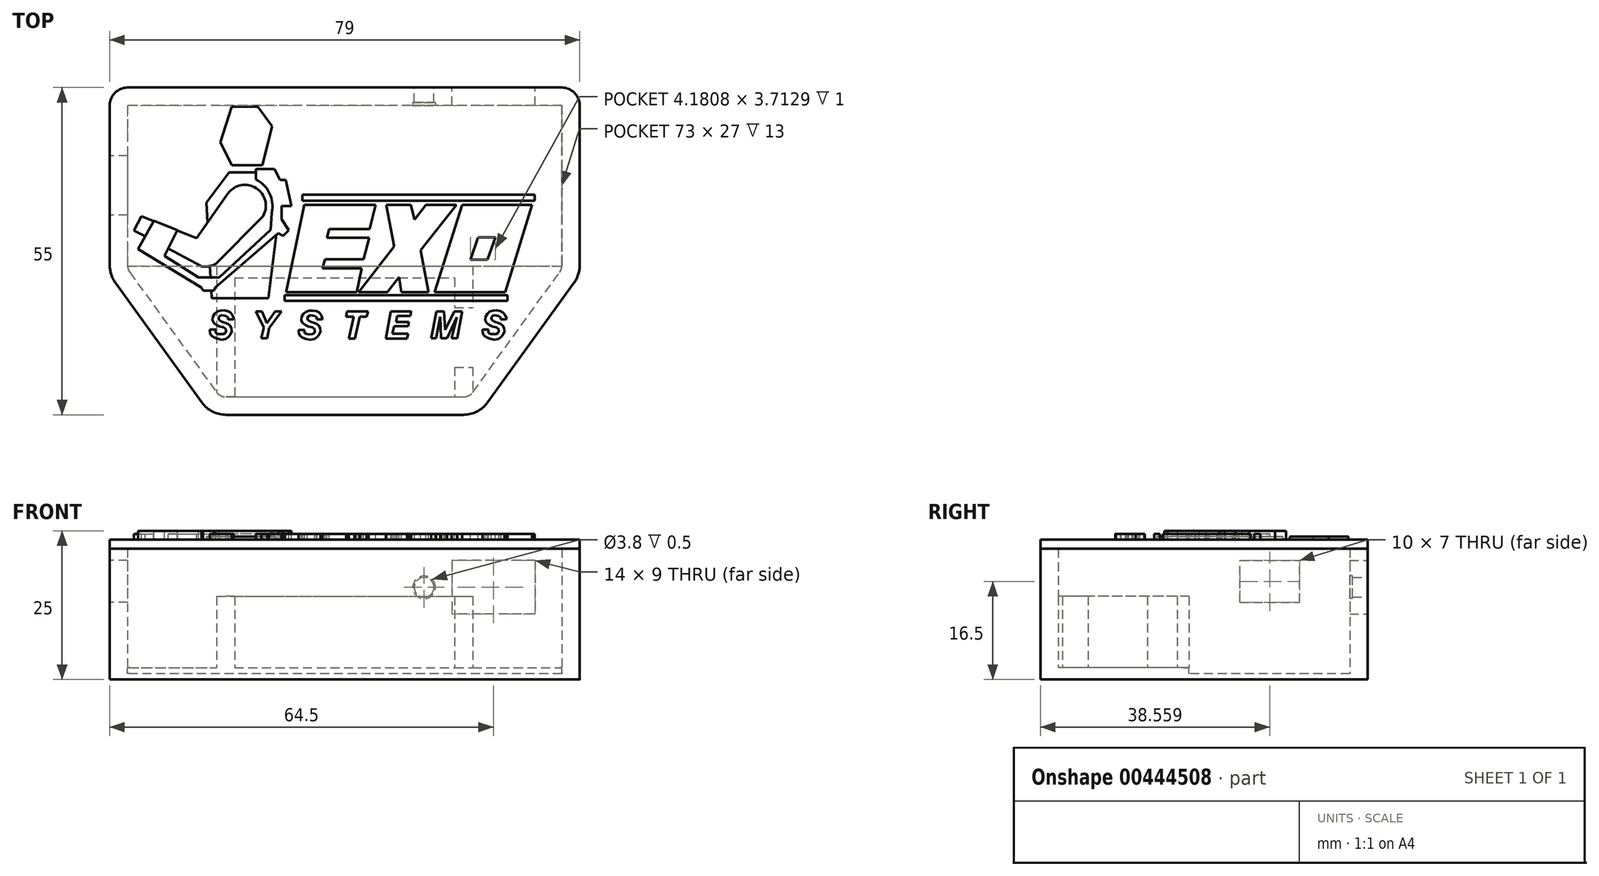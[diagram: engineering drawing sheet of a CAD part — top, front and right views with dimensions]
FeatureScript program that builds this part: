
annotation { "Feature Type Name" : "Feature", "Feature Type Description" : "" }
export const myFeature = defineFeature(function(context is Context, id is Id, definition is map)
    precondition{}
    {
        {
            var Q0;
            Q0=qCreatedBy(makeId("Top.planeOp"),FACE);
            var sketch = newSketch(context, id + "F0", { "sketchPlane" : qUnion([Q0])});
            skLineSegment(sketch, "E0", {"start": v(67, 30) * mm, "end": v(-67, 30) * mm, "construction": true});
            skPoint(sketch, "E1", {"position": v(0, -28) * mm});
            skPoint(sketch, "E2", {"position": v(0, 30) * mm});
            skLineSegment(sketch, "E3.0", {"start": v(36.5, 27) * mm, "end": v(-36.5, 27) * mm});
            skPoint(sketch, "E4.visualSharp", {"position": v(-61.92, 27) * mm});
            skPoint(sketch, "E5.visualSharp", {"position": v(61.92, 27) * mm});
            skLineSegment(sketch, "E6", {"start": v(39.5, 24) * mm, "end": v(39.5, -2.88) * mm});
            skLineSegment(sketch, "E7", {"start": v(38.55, -5.81) * mm, "end": v(24, -25.93) * mm});
            skLineSegment(sketch, "E8", {"start": v(19.95, -28) * mm, "end": v(0, -28) * mm});
            skPoint(sketch, "E9.visualSharp", {"position": v(39.5, -4.5) * mm});
            skArc(sketch, "E9.filletArc", {"start": v(38.55, -5.81) * mm, "mid": v(39.26, -4.42) * mm, "end": v(39.5, -2.88) * mm});
            skPoint(sketch, "E10.visualSharp", {"position": v(22.5, -28) * mm});
            skArc(sketch, "E10.filletArc", {"start": v(19.95, -28) * mm, "mid": v(22.22, -27.45) * mm, "end": v(24, -25.93) * mm});
            skLineSegment(sketch, "E11.MirrorCS", {"start": v(-39.5, 24) * mm, "end": v(-39.5, -2.88) * mm});
            skLineSegment(sketch, "E12.MirrorCS", {"start": v(-38.55, -5.81) * mm, "end": v(-24, -25.93) * mm});
            skLineSegment(sketch, "E13.MirrorCS", {"start": v(-19.95, -28) * mm, "end": v(0, -28) * mm});
            skArc(sketch, "E14.MirrorCS", {"start": v(-19.95, -28) * mm, "mid": v(-22.22, -27.45) * mm, "end": v(-24, -25.93) * mm});
            skArc(sketch, "E15.MirrorCS", {"start": v(-38.55, -5.81) * mm, "mid": v(-39.26, -4.42) * mm, "end": v(-39.5, -2.88) * mm});
            skPoint(sketch, "E16.visualSharp", {"position": v(-39.5, 27) * mm});
            skArc(sketch, "E16.filletArc", {"start": v(-36.5, 27) * mm, "mid": v(-38.62, 26.12) * mm, "end": v(-39.5, 24) * mm});
            skPoint(sketch, "E17.visualSharp", {"position": v(39.5, 27) * mm});
            skArc(sketch, "E17.filletArc", {"start": v(39.5, 24) * mm, "mid": v(38.62, 26.12) * mm, "end": v(36.5, 27) * mm});
            skSolve(sketch);
        }
        {
            var Q0;
            Q0=makeQuery(id+"F0.imprint","IMPRINT",FACE,{"disambiguationData":[TD([[makeQuery(id+"F0.imprint","IMPRINT",EDGE,{"derivedFrom":sQuery(id+"F0.wireOp",EDGE,"E3.0")}),1.0]])]});
            extrude(context, id + "F1", {"entities" : qUnion([Q0]), "depth" : 2 * mm});
        }
        {
            var Q0;
            Q0=makeQuery(id+"F1.opExtrude","CAP_FACE",FACE,{"disambiguationData":[OSD([sQuery(id+"F0.wireOp",EDGE,"E3.0"),sQuery(id+"F0.wireOp",EDGE,"E3.1"),sQuery(id+"F0.wireOp",EDGE,"E3.2"),sQuery(id+"F0.wireOp",EDGE,"E3.3"),sQuery(id+"F0.wireOp",EDGE,"E4.filletArc"),sQuery(id+"F0.wireOp",EDGE,"E5.filletArc"),sQuery(id+"F0.wireOp",EDGE,"62008701-16d0-4b05-af1f-bc20bacb61fe.filletArc"),sQuery(id+"F0.wireOp",EDGE,"d9b4f20a-ce9e-42cc-84f3-acf8152c3e49.filletArc")])],"isStart":false});
            var sketch = newSketch(context, id + "F2", { "sketchPlane" : qUnion([Q0])});
            skArc(sketch, "E18.0.0", {"start": v(-24, -25.93) * mm, "mid": v(-22.22, -27.45) * mm, "end": v(-19.95, -28) * mm});
            skLineSegment(sketch, "E18.0.1", {"start": v(-19.95, -28) * mm, "end": v(19.95, -28) * mm});
            skArc(sketch, "E18.0.2", {"start": v(19.95, -28) * mm, "mid": v(22.22, -27.45) * mm, "end": v(24, -25.93) * mm});
            skLineSegment(sketch, "E18.0.3", {"start": v(24, -25.93) * mm, "end": v(38.55, -5.81) * mm});
            skArc(sketch, "E18.0.4", {"start": v(38.55, -5.81) * mm, "mid": v(39.26, -4.42) * mm, "end": v(39.5, -2.88) * mm});
            skLineSegment(sketch, "E18.0.5", {"start": v(39.5, -2.88) * mm, "end": v(39.5, 24) * mm});
            skArc(sketch, "E18.0.6", {"start": v(39.5, 24) * mm, "mid": v(38.62, 26.12) * mm, "end": v(36.5, 27) * mm});
            skLineSegment(sketch, "E18.0.7", {"start": v(36.5, 27) * mm, "end": v(-36.5, 27) * mm});
            skArc(sketch, "E18.0.8", {"start": v(-36.5, 27) * mm, "mid": v(-38.62, 26.12) * mm, "end": v(-39.5, 24) * mm});
            skLineSegment(sketch, "E18.0.9", {"start": v(-39.5, 24) * mm, "end": v(-39.5, -2.88) * mm});
            skArc(sketch, "E18.0.10", {"start": v(-39.5, -2.88) * mm, "mid": v(-39.26, -4.42) * mm, "end": v(-38.55, -5.81) * mm});
            skLineSegment(sketch, "E18.0.11", {"start": v(-38.55, -5.81) * mm, "end": v(-24, -25.93) * mm});
            skLineSegment(sketch, "E19.0", {"start": v(36.5, 24) * mm, "end": v(36.5, 24) * mm});
            skLineSegment(sketch, "E19.1", {"start": v(-36.12, -4.05) * mm, "end": v(-21.57, -24.17) * mm});
            skArc(sketch, "E19.2", {"start": v(-36.5, -2.88) * mm, "mid": v(-36.4, -3.5) * mm, "end": v(-36.12, -4.05) * mm});
            skLineSegment(sketch, "E19.3", {"start": v(-36.5, 24) * mm, "end": v(-36.5, -2.88) * mm});
            skLineSegment(sketch, "E19.4", {"start": v(-36.5, 24) * mm, "end": v(-36.5, 24) * mm});
            skArc(sketch, "E19.5", {"start": v(-21.57, -24.17) * mm, "mid": v(-20.86, -24.78) * mm, "end": v(-19.95, -25) * mm});
            skLineSegment(sketch, "E19.6", {"start": v(36.5, 24) * mm, "end": v(-36.5, 24) * mm});
            skLineSegment(sketch, "E19.7", {"start": v(-19.95, -25) * mm, "end": v(19.95, -25) * mm});
            skArc(sketch, "E19.8", {"start": v(19.95, -25) * mm, "mid": v(20.86, -24.78) * mm, "end": v(21.57, -24.17) * mm});
            skLineSegment(sketch, "E19.9", {"start": v(21.57, -24.17) * mm, "end": v(36.12, -4.05) * mm});
            skArc(sketch, "E19.10", {"start": v(36.12, -4.05) * mm, "mid": v(36.4, -3.5) * mm, "end": v(36.5, -2.88) * mm});
            skLineSegment(sketch, "E19.11", {"start": v(36.5, -2.88) * mm, "end": v(36.5, 24) * mm});
            skSolve(sketch);
        }
        {
            var Q0;
            Q0 = qSketchRegion(id + "F2", true);
            extrude(context, id + "F3", {"entities" : qUnion([Q0]), "operationType" : NewBodyOperationType.ADD, "depth" : 20 * mm});
        }
        {
            var Q0;
            Q0=makeQuery(id+"F1.opExtrude","CAP_FACE",FACE,{"disambiguationData":[OSD([sQuery(id+"F0.wireOp",EDGE,"E3.0"),sQuery(id+"F0.wireOp",EDGE,"E3.1"),sQuery(id+"F0.wireOp",EDGE,"E3.2"),sQuery(id+"F0.wireOp",EDGE,"E3.3"),sQuery(id+"F0.wireOp",EDGE,"E4.filletArc"),sQuery(id+"F0.wireOp",EDGE,"E5.filletArc"),sQuery(id+"F0.wireOp",EDGE,"62008701-16d0-4b05-af1f-bc20bacb61fe.filletArc"),sQuery(id+"F0.wireOp",EDGE,"d9b4f20a-ce9e-42cc-84f3-acf8152c3e49.filletArc")])],"isStart":false});
            var sketch = newSketch(context, id + "F4", { "sketchPlane" : qUnion([Q0])});
            skLineSegment(sketch, "E20", {"start": v(0, 0) * mm, "end": v(0, -63.6) * mm, "construction": true});
            skLineSegment(sketch, "E21.bottom", {"start": v(-18.5, -5) * mm, "end": v(18.5, -5) * mm});
            skLineSegment(sketch, "E21.top", {"start": v(-18.5, -25) * mm, "end": v(18.5, -25) * mm});
            skLineSegment(sketch, "E21.left", {"start": v(-18.5, -5) * mm, "end": v(-18.5, -25) * mm});
            skLineSegment(sketch, "E21.right", {"start": v(18.5, -5) * mm, "end": v(18.5, -10) * mm});
            skPoint(sketch, "E21.middle", {"position": v(0, -15) * mm});
            skLineSegment(sketch, "E22.bottom", {"start": v(-21.5, -3) * mm, "end": v(21.5, -3) * mm});
            skLineSegment(sketch, "E22.left", {"start": v(-21.5, -3) * mm, "end": v(-21.5, -25) * mm});
            skLineSegment(sketch, "E22.right", {"start": v(21.5, -3) * mm, "end": v(21.5, -10) * mm});
            skLineSegment(sketch, "E23", {"start": v(18.5, -25) * mm, "end": v(21.5, -25) * mm});
            skLineSegment(sketch, "E24", {"start": v(-18.5, -25) * mm, "end": v(-21.5, -25) * mm});
            skLineSegment(sketch, "E25.0", {"start": v(21.57, -24.17) * mm, "end": v(36.12, -4.05) * mm, "construction": true});
            skLineSegment(sketch, "E26.0", {"start": v(-36.12, -4.05) * mm, "end": v(-21.57, -24.17) * mm, "construction": true});
            skLineSegment(sketch, "E27.0", {"start": v(-19.95, -25) * mm, "end": v(19.95, -25) * mm, "construction": true});
            skPoint(sketch, "E28", {"position": v(18.5, -15) * mm});
            skLineSegment(sketch, "E29", {"start": v(18.5, -10) * mm, "end": v(21.5, -10) * mm});
            skLineSegment(sketch, "E30", {"start": v(18.5, -20) * mm, "end": v(21.5, -20) * mm});
            skLineSegment(sketch, "E31.trimOffspring", {"start": v(21.5, -20) * mm, "end": v(21.5, -25) * mm});
            skLineSegment(sketch, "E32.trimOffspring", {"start": v(18.5, -20) * mm, "end": v(18.5, -25) * mm});
            skSolve(sketch);
        }
        {
            var Q0;
            Q0 = qSketchRegion(id + "F4", true);
            extrude(context, id + "F5", {"entities" : qUnion([Q0]), "operationType" : NewBodyOperationType.ADD, "depth" : 12 * mm});
        }
        {
            var Q0;
            Q0=makeQuery(id+"F3.boolean.opBoolean","MERGE",FACE,{"derivedFrom":[makeQuery(id+"F1.opExtrude","SWEPT_FACE",FACE,{"disambiguationData":[OSD([sQuery(id+"F0.wireOp",EDGE,"E3.0")])]}),makeQuery(id+"F3.opExtrude","SWEPT_FACE",FACE,{"disambiguationData":[OSD([sQuery(id+"F2.wireOp",EDGE,"d3a6f8c1-4bed-4510-b358-771d81ea86e4.0.5")])]})]});
            var sketch = newSketch(context, id + "F6", { "sketchPlane" : qUnion([Q0])});
            skLineSegment(sketch, "E33.bottom", {"start": v(-32, 20) * mm, "end": v(-18, 20) * mm});
            skLineSegment(sketch, "E33.top", {"start": v(-32, 11) * mm, "end": v(-18, 11) * mm});
            skLineSegment(sketch, "E33.left", {"start": v(-32, 20) * mm, "end": v(-32, 11) * mm});
            skLineSegment(sketch, "E33.right", {"start": v(-18, 20) * mm, "end": v(-18, 11) * mm});
            skLineSegment(sketch, "E34.bottom", {"start": v(-33.5, 21) * mm, "end": v(-16.5, 21) * mm, "construction": true});
            skLineSegment(sketch, "E34.top", {"start": v(-33.5, 10) * mm, "end": v(-16.5, 10) * mm, "construction": true});
            skLineSegment(sketch, "E34.left", {"start": v(-33.5, 21) * mm, "end": v(-33.5, 10) * mm, "construction": true});
            skLineSegment(sketch, "E34.right", {"start": v(-16.5, 21) * mm, "end": v(-16.5, 10) * mm, "construction": true});
            skPoint(sketch, "E35", {"position": v(-32, 15.5) * mm});
            skLineSegment(sketch, "E36.0", {"start": v(-36.5, 18.1) * mm, "end": v(-36.5, 0) * mm, "construction": true});
            skCircle(sketch, "E37", {"center": v(-13.35, 15.5) * mm, "radius": 1.65 * mm});
            skLineSegment(sketch, "E38.0", {"start": v(-36.5, 22) * mm, "end": v(36.5, 22) * mm, "construction": true});
            skSolve(sketch);
        }
        {
            var Q0;
            Q0 = qSketchRegion(id + "F6", true);
            var Q1;
            Q1=makeQuery(id+"F3.opExtrude","SWEPT_FACE",FACE,{"disambiguationData":[OSD([sQuery(id+"F2.wireOp",EDGE,"E19.6")])]});
            extrude(context, id + "F7", {"entities" : qUnion([Q0]), "operationType" : NewBodyOperationType.REMOVE, "endBound" : BoundingType.UP_TO_SURFACE, "oppositeDirection" : true, "endBoundEntityFace" : qUnion([Q1]), "depth" : 25 * mm});
        }
        {
            var Q0;
            Q0=qCreatedBy(makeId("Right.planeOp"),FACE);
            cPlane(context, id + "F8", {"entities" : qUnion([Q0]), "cplaneType" : CPlaneType.OFFSET, "offset" : 48 * mm, "oppositeDirection" : true, "width" : 150 * mm, "height" : 150 * mm});
        }
        {
            var Q0;
            Q0=qCreatedBy(id+"F8.planeOp",FACE);
            var sketch = newSketch(context, id + "F9", { "sketchPlane" : qUnion([Q0])});
            skLineSegment(sketch, "E39.bottom", {"start": v(15.56, 20) * mm, "end": v(5.56, 20) * mm});
            skLineSegment(sketch, "E39.top", {"start": v(15.56, 13) * mm, "end": v(5.56, 13) * mm});
            skLineSegment(sketch, "E39.left", {"start": v(15.56, 20) * mm, "end": v(15.56, 13) * mm});
            skLineSegment(sketch, "E39.right", {"start": v(5.56, 20) * mm, "end": v(5.56, 13) * mm});
            skPoint(sketch, "E39.middle", {"position": v(10.56, 16.5) * mm});
            skPoint(sketch, "E40", {"position": v(15.56, 16.5) * mm});
            skLineSegment(sketch, "E41.0", {"start": v(24, 22) * mm, "end": v(-2.88, 22) * mm, "construction": true});
            skPoint(sketch, "E42", {"position": v(10.56, 22) * mm});
            skPoint(sketch, "E43", {"position": v(10.56, 20) * mm});
            skLineSegment(sketch, "E44", {"start": v(10.56, 22) * mm, "end": v(10.56, 20) * mm, "construction": true});
            skSolve(sketch);
        }
        {
            var Q0;
            Q0 = qSketchRegion(id + "F9", true);
            var Q1;
            Q1=makeQuery(id+"F3.opExtrude","SWEPT_FACE",FACE,{"disambiguationData":[OSD([sQuery(id+"F2.wireOp",EDGE,"E19.3")])]});
            extrude(context, id + "F10", {"entities" : qUnion([Q0]), "operationType" : NewBodyOperationType.REMOVE, "endBound" : BoundingType.UP_TO_SURFACE, "endBoundEntityFace" : qUnion([Q1]), "depth" : 20.2 * mm});
        }
        {
            var Q0;
            Q0=makeQuery(id+"F1.opExtrude","CAP_FACE",FACE,{"disambiguationData":[OSD([sQuery(id+"F0.wireOp",EDGE,"E3.0"),sQuery(id+"F0.wireOp",EDGE,"E6"),sQuery(id+"F0.wireOp",EDGE,"E7"),sQuery(id+"F0.wireOp",EDGE,"E8"),sQuery(id+"F0.wireOp",EDGE,"E9.filletArc"),sQuery(id+"F0.wireOp",EDGE,"E10.filletArc"),sQuery(id+"F0.wireOp",EDGE,"E11.MirrorCS"),sQuery(id+"F0.wireOp",EDGE,"E12.MirrorCS"),sQuery(id+"F0.wireOp",EDGE,"E13.MirrorCS"),sQuery(id+"F0.wireOp",EDGE,"E14.MirrorCS"),sQuery(id+"F0.wireOp",EDGE,"E15.MirrorCS"),sQuery(id+"F0.wireOp",EDGE,"E16.filletArc"),sQuery(id+"F0.wireOp",EDGE,"E17.filletArc")])],"isStart":false});
            var sketch = newSketch(context, id + "F11", { "sketchPlane" : qUnion([Q0])});
            skLineSegment(sketch, "E45.bottom", {"start": v(-36.5, 24) * mm, "end": v(36.5, 24) * mm});
            skLineSegment(sketch, "E45.top", {"start": v(-36.5, -3) * mm, "end": v(36.5, -3) * mm});
            skLineSegment(sketch, "E45.left", {"start": v(-36.5, 24) * mm, "end": v(-36.5, -3) * mm});
            skLineSegment(sketch, "E45.right", {"start": v(36.5, 24) * mm, "end": v(36.5, -3) * mm});
            skSolve(sketch);
        }
        {
            var Q0;
            Q0 = qSketchRegion(id + "F11", true);
            extrude(context, id + "F12", {"entities" : qUnion([Q0]), "operationType" : NewBodyOperationType.REMOVE, "oppositeDirection" : true, "depth" : 1 * mm});
        }
        {
            var Q0;
            Q0=makeQuery(id+"F12.boolean.opBoolean","MERGE",FACE,{"derivedFrom":[makeQuery(id+"F3.opExtrude","SWEPT_FACE",FACE,{"disambiguationData":[OSD([sQuery(id+"F2.wireOp",EDGE,"E19.6")])]}),makeQuery(id+"F12.opExtrude","SWEPT_FACE",FACE,{"disambiguationData":[OSD([sQuery(id+"F11.wireOp",EDGE,"E45.bottom")])]})]});
            var sketch = newSketch(context, id + "F13", { "sketchPlane" : qUnion([Q0])});
            skCircle(sketch, "E46.0", {"center": v(13.35, 15.5) * mm, "radius": 1.65 * mm});
            skCircle(sketch, "E47", {"center": v(13.35, 15.5) * mm, "radius": 1.9 * mm});
            skSolve(sketch);
        }
        {
            var Q0;
            Q0 = qSketchRegion(id + "F13", true);
            extrude(context, id + "F14", {"entities" : qUnion([Q0]), "operationType" : NewBodyOperationType.REMOVE, "oppositeDirection" : true, "depth" : 0.5 * mm});
        }
        {
            var Q0;
            Q0=makeQuery(id+"F3.opExtrude","CAP_FACE",FACE,{"disambiguationData":[OSD([sQuery(id+"F2.wireOp",EDGE,"E18.0.0"),sQuery(id+"F2.wireOp",EDGE,"E18.0.1"),sQuery(id+"F2.wireOp",EDGE,"E18.0.2"),sQuery(id+"F2.wireOp",EDGE,"E18.0.3"),sQuery(id+"F2.wireOp",EDGE,"E18.0.4"),sQuery(id+"F2.wireOp",EDGE,"E18.0.5"),sQuery(id+"F2.wireOp",EDGE,"E18.0.6"),sQuery(id+"F2.wireOp",EDGE,"E18.0.7"),sQuery(id+"F2.wireOp",EDGE,"E18.0.8"),sQuery(id+"F2.wireOp",EDGE,"E18.0.9"),sQuery(id+"F2.wireOp",EDGE,"E18.0.10"),sQuery(id+"F2.wireOp",EDGE,"E18.0.11"),sQuery(id+"F2.wireOp",EDGE,"E19.1"),sQuery(id+"F2.wireOp",EDGE,"E19.2"),sQuery(id+"F2.wireOp",EDGE,"E19.3"),sQuery(id+"F2.wireOp",EDGE,"E19.5"),sQuery(id+"F2.wireOp",EDGE,"E19.6"),sQuery(id+"F2.wireOp",EDGE,"E19.7"),sQuery(id+"F2.wireOp",EDGE,"E19.8"),sQuery(id+"F2.wireOp",EDGE,"E19.9"),sQuery(id+"F2.wireOp",EDGE,"E19.10"),sQuery(id+"F2.wireOp",EDGE,"E19.11")])],"isStart":false});
            var sketch = newSketch(context, id + "F15", { "sketchPlane" : qUnion([Q0])});
            skLineSegment(sketch, "E48.0", {"start": v(36.5, 27) * mm, "end": v(-36.5, 27) * mm});
            skArc(sketch, "E49.0", {"start": v(-36.5, 27) * mm, "mid": v(-38.62, 26.12) * mm, "end": v(-39.5, 24) * mm});
            skLineSegment(sketch, "E50.0", {"start": v(-39.5, 24) * mm, "end": v(-39.5, -2.88) * mm});
            skArc(sketch, "E51.0", {"start": v(-38.55, -5.81) * mm, "mid": v(-39.26, -4.42) * mm, "end": v(-39.5, -2.88) * mm});
            skLineSegment(sketch, "E52.0", {"start": v(-38.55, -5.81) * mm, "end": v(-24, -25.93) * mm});
            skArc(sketch, "E53.0", {"start": v(-19.95, -28) * mm, "mid": v(-22.22, -27.45) * mm, "end": v(-24, -25.93) * mm});
            skLineSegment(sketch, "E54.0", {"start": v(-19.95, -28) * mm, "end": v(19.95, -28) * mm});
            skArc(sketch, "E55.0", {"start": v(19.95, -28) * mm, "mid": v(22.22, -27.45) * mm, "end": v(24, -25.93) * mm});
            skLineSegment(sketch, "E56.0", {"start": v(38.55, -5.81) * mm, "end": v(24, -25.93) * mm});
            skPoint(sketch, "E57.0", {"position": v(39.26, -4.42) * mm});
            skArc(sketch, "E58.0", {"start": v(38.55, -5.81) * mm, "mid": v(39.26, -4.42) * mm, "end": v(39.5, -2.88) * mm});
            skLineSegment(sketch, "E59.0", {"start": v(39.5, 24) * mm, "end": v(39.5, -2.88) * mm});
            skArc(sketch, "E60.0", {"start": v(39.5, 24) * mm, "mid": v(38.62, 26.12) * mm, "end": v(36.5, 27) * mm});
            skSolve(sketch);
        }
        {
            var Q0;
            Q0 = qSketchRegion(id + "F15", true);
            extrude(context, id + "F16", {"entities" : qUnion([Q0]), "depth" : 1.5 * mm});
        }
        {
            var Q0;
            Q0=makeQuery(id+"F16.opExtrude","CAP_FACE",FACE,{"disambiguationData":[OSD([sQuery(id+"F15.wireOp",EDGE,"E48.0"),sQuery(id+"F15.wireOp",EDGE,"E49.0"),sQuery(id+"F15.wireOp",EDGE,"E50.0"),sQuery(id+"F15.wireOp",EDGE,"E51.0"),sQuery(id+"F15.wireOp",EDGE,"E52.0"),sQuery(id+"F15.wireOp",EDGE,"E53.0"),sQuery(id+"F15.wireOp",EDGE,"E54.0"),sQuery(id+"F15.wireOp",EDGE,"E55.0"),sQuery(id+"F15.wireOp",EDGE,"E56.0"),sQuery(id+"F15.wireOp",EDGE,"E58.0"),sQuery(id+"F15.wireOp",EDGE,"E59.0"),sQuery(id+"F15.wireOp",EDGE,"E60.0")])],"isStart":false});
            var sketch = newSketch(context, id + "F17", { "sketchPlane" : qUnion([Q0])});
            skPoint(sketch, "E61", {"position": v(0, 27) * mm});
            skLineSegment(sketch, "E62", {"start": v(-18.97, 23.76) * mm, "end": v(-20.88, 17.84) * mm});
            skLineSegment(sketch, "E63", {"start": v(-20.88, 17.84) * mm, "end": v(-18.97, 13.96) * mm});
            skLineSegment(sketch, "E64", {"start": v(-18.97, 13.96) * mm, "end": v(-13.82, 13.96) * mm});
            skLineSegment(sketch, "E65", {"start": v(-13.82, 13.96) * mm, "end": v(-12.19, 20.46) * mm});
            skLineSegment(sketch, "E66", {"start": v(-12.19, 20.46) * mm, "end": v(-14.6, 23.76) * mm});
            skLineSegment(sketch, "E67", {"start": v(-14.6, 23.76) * mm, "end": v(-18.97, 23.76) * mm});
            skLineSegment(sketch, "E68", {"start": v(-23.25, 7.69) * mm, "end": v(-22.38, -8.4) * mm});
            skLineSegment(sketch, "E69", {"start": v(-22.38, -8.4) * mm, "end": v(-12.85, -8.4) * mm});
            skLineSegment(sketch, "E70", {"start": v(-12.85, -8.4) * mm, "end": v(-11.17, 4.8) * mm});
            skLineSegment(sketch, "E71", {"start": v(-11.17, 4.8) * mm, "end": v(-11.17, 10.03) * mm});
            skLineSegment(sketch, "E72", {"start": v(-12.5, 12.71) * mm, "end": v(-11.17, 10.03) * mm});
            skLineSegment(sketch, "E73", {"start": v(-12.5, 12.71) * mm, "end": v(-19.45, 12.71) * mm});
            skLineSegment(sketch, "E74", {"start": v(-19.45, 12.71) * mm, "end": v(-23.25, 7.69) * mm});
            skLineSegment(sketch, "E75.bottom", {"start": v(-7.13, 7.99) * mm, "end": v(31.95, 7.99) * mm});
            skLineSegment(sketch, "E75.top", {"start": v(-7.13, 8.99) * mm, "end": v(31.95, 8.99) * mm});
            skLineSegment(sketch, "E75.left", {"start": v(-7.13, 7.99) * mm, "end": v(-7.13, 8.99) * mm});
            skLineSegment(sketch, "E75.right", {"start": v(31.95, 7.99) * mm, "end": v(31.95, 8.99) * mm});
            skLineSegment(sketch, "E76.bottom", {"start": v(-10.12, -7.88) * mm, "end": v(27.39, -7.88) * mm});
            skLineSegment(sketch, "E76.top", {"start": v(-10.12, -8.88) * mm, "end": v(27.39, -8.88) * mm});
            skLineSegment(sketch, "E76.left", {"start": v(-10.12, -7.88) * mm, "end": v(-10.12, -8.88) * mm});
            skLineSegment(sketch, "E76.right", {"start": v(27.39, -7.88) * mm, "end": v(27.39, -8.88) * mm});
            skLineSegment(sketch, "E77", {"start": v(-6.81, 7.3) * mm, "end": v(-9.83, -7.39) * mm});
            skLineSegment(sketch, "E78", {"start": v(-9.83, -7.39) * mm, "end": v(2.03, -7.39) * mm});
            skLineSegment(sketch, "E79", {"start": v(2.03, -7.39) * mm, "end": v(2.86, -3.37) * mm});
            skLineSegment(sketch, "E80", {"start": v(2.86, -3.37) * mm, "end": v(-3.77, -3.37) * mm});
            skLineSegment(sketch, "E81", {"start": v(-3.77, -3.37) * mm, "end": v(-3.32, -1.85) * mm});
            skLineSegment(sketch, "E82", {"start": v(-3.32, -1.85) * mm, "end": v(3.16, -1.85) * mm});
            skLineSegment(sketch, "E83", {"start": v(3.16, -1.85) * mm, "end": v(4.1, 1.74) * mm});
            skLineSegment(sketch, "E84", {"start": v(4.1, 1.74) * mm, "end": v(-3, 1.74) * mm});
            skLineSegment(sketch, "E85", {"start": v(-3, 1.74) * mm, "end": v(-2.6, 3.23) * mm});
            skLineSegment(sketch, "E86", {"start": v(-2.6, 3.23) * mm, "end": v(4.16, 3.23) * mm});
            skLineSegment(sketch, "E87", {"start": v(-6.81, 7.3) * mm, "end": v(5.19, 7.3) * mm});
            skLineSegment(sketch, "E88", {"start": v(5.19, 7.3) * mm, "end": v(4.16, 3.23) * mm});
            skLineSegment(sketch, "E89", {"start": v(6.97, 7.3) * mm, "end": v(8.31, 0.32) * mm});
            skLineSegment(sketch, "E90", {"start": v(8.31, 0.32) * mm, "end": v(2.35, -7.39) * mm});
            skLineSegment(sketch, "E91", {"start": v(2.35, -7.39) * mm, "end": v(7.16, -7.39) * mm});
            skLineSegment(sketch, "E92", {"start": v(7.16, -7.39) * mm, "end": v(9.14, -4.85) * mm});
            skLineSegment(sketch, "E93", {"start": v(9.14, -4.85) * mm, "end": v(9.52, -7.39) * mm});
            skLineSegment(sketch, "E94", {"start": v(9.52, -7.39) * mm, "end": v(14.1, -7.39) * mm});
            skLineSegment(sketch, "E95", {"start": v(14.1, -7.39) * mm, "end": v(12.74, -0.31) * mm});
            skLineSegment(sketch, "E96", {"start": v(12.74, -0.31) * mm, "end": v(18.8, 7.3) * mm});
            skLineSegment(sketch, "E97", {"start": v(18.8, 7.3) * mm, "end": v(13.63, 7.3) * mm});
            skLineSegment(sketch, "E98", {"start": v(13.63, 7.3) * mm, "end": v(11.74, 4.8) * mm});
            skLineSegment(sketch, "E99", {"start": v(11.74, 4.8) * mm, "end": v(11.1, 7.3) * mm});
            skLineSegment(sketch, "E100", {"start": v(11.1, 7.3) * mm, "end": v(6.97, 7.3) * mm});
            skLineSegment(sketch, "E101", {"start": v(19.77, 7.3) * mm, "end": v(15.14, -7.39) * mm});
            skLineSegment(sketch, "E102", {"start": v(15.14, -7.39) * mm, "end": v(26.97, -7.39) * mm});
            skLineSegment(sketch, "E103", {"start": v(26.97, -7.39) * mm, "end": v(31.46, 7.3) * mm});
            skLineSegment(sketch, "E104", {"start": v(31.46, 7.3) * mm, "end": v(19.77, 7.3) * mm});
            skLineSegment(sketch, "E105", {"start": v(22.44, 1.8) * mm, "end": v(21.14, -1.91) * mm});
            skLineSegment(sketch, "E106", {"start": v(21.14, -1.91) * mm, "end": v(23.97, -1.91) * mm});
            skLineSegment(sketch, "E107", {"start": v(23.97, -1.91) * mm, "end": v(25.32, 1.8) * mm});
            skLineSegment(sketch, "E108", {"start": v(25.32, 1.8) * mm, "end": v(22.44, 1.8) * mm});
            skLineSegment(sketch, "E109", {"start": v(-14.91, -10.63) * mm, "end": v(-13.57, -13.38) * mm});
            skLineSegment(sketch, "E110", {"start": v(-13.57, -13.38) * mm, "end": v(-14, -15.16) * mm});
            skLineSegment(sketch, "E111", {"start": v(-14, -15.16) * mm, "end": v(-13.01, -15.16) * mm});
            skLineSegment(sketch, "E112", {"start": v(-13.01, -15.16) * mm, "end": v(-12.7, -13.44) * mm});
            skLineSegment(sketch, "E113", {"start": v(-12.7, -13.44) * mm, "end": v(-10.61, -10.65) * mm});
            skLineSegment(sketch, "E114", {"start": v(-10.61, -10.65) * mm, "end": v(-11.7, -10.65) * mm});
            skLineSegment(sketch, "E115", {"start": v(-11.7, -10.65) * mm, "end": v(-13.07, -12.6) * mm});
            skLineSegment(sketch, "E116", {"start": v(-14.91, -10.63) * mm, "end": v(-13.89, -10.63) * mm});
            skLineSegment(sketch, "E117", {"start": v(-13.89, -10.63) * mm, "end": v(-13.07, -12.6) * mm});
            skLineSegment(sketch, "E118", {"start": v(0.36, -10.64) * mm, "end": v(0.24, -11.5) * mm});
            skLineSegment(sketch, "E119", {"start": v(0.24, -11.5) * mm, "end": v(1.53, -11.5) * mm});
            skLineSegment(sketch, "E120", {"start": v(1.53, -11.5) * mm, "end": v(0.72, -15.22) * mm});
            skLineSegment(sketch, "E121", {"start": v(0.72, -15.22) * mm, "end": v(1.7, -15.22) * mm});
            skLineSegment(sketch, "E122", {"start": v(1.7, -15.22) * mm, "end": v(2.52, -11.5) * mm});
            skLineSegment(sketch, "E123", {"start": v(2.52, -11.5) * mm, "end": v(3.7, -11.5) * mm});
            skLineSegment(sketch, "E124", {"start": v(0.36, -10.64) * mm, "end": v(3.92, -10.64) * mm});
            skLineSegment(sketch, "E125", {"start": v(3.92, -10.64) * mm, "end": v(3.7, -11.5) * mm});
            skLineSegment(sketch, "E126", {"start": v(7.75, -10.64) * mm, "end": v(6.93, -15.18) * mm});
            skLineSegment(sketch, "E127", {"start": v(6.93, -15.18) * mm, "end": v(10.49, -15.18) * mm});
            skLineSegment(sketch, "E128", {"start": v(10.49, -15.18) * mm, "end": v(10.65, -14.37) * mm});
            skLineSegment(sketch, "E129", {"start": v(10.65, -14.37) * mm, "end": v(8, -14.37) * mm});
            skLineSegment(sketch, "E130", {"start": v(8, -14.37) * mm, "end": v(8.29, -13.12) * mm});
            skLineSegment(sketch, "E131", {"start": v(8.29, -13.12) * mm, "end": v(10.67, -13.12) * mm});
            skLineSegment(sketch, "E132", {"start": v(10.67, -13.12) * mm, "end": v(10.8, -12.38) * mm});
            skLineSegment(sketch, "E133", {"start": v(10.8, -12.38) * mm, "end": v(8.64, -12.38) * mm});
            skLineSegment(sketch, "E134", {"start": v(8.64, -12.38) * mm, "end": v(8.85, -11.38) * mm});
            skLineSegment(sketch, "E135", {"start": v(8.85, -11.38) * mm, "end": v(11.01, -11.38) * mm});
            skLineSegment(sketch, "E136", {"start": v(11.01, -11.38) * mm, "end": v(11.15, -10.64) * mm});
            skLineSegment(sketch, "E137", {"start": v(11.15, -10.64) * mm, "end": v(7.75, -10.64) * mm});
            skLineSegment(sketch, "E138", {"start": v(15.4, -10.64) * mm, "end": v(14.51, -15.15) * mm});
            skLineSegment(sketch, "E139", {"start": v(14.51, -15.15) * mm, "end": v(15.37, -15.15) * mm});
            skLineSegment(sketch, "E140", {"start": v(15.37, -15.15) * mm, "end": v(16.08, -11.5) * mm});
            skLineSegment(sketch, "E141", {"start": v(16.08, -11.5) * mm, "end": v(16.2, -15.14) * mm});
            skLineSegment(sketch, "E142", {"start": v(16.2, -15.14) * mm, "end": v(17.18, -15.14) * mm});
            skLineSegment(sketch, "E143", {"start": v(17.18, -15.14) * mm, "end": v(18.87, -11.55) * mm});
            skLineSegment(sketch, "E144", {"start": v(18.87, -11.55) * mm, "end": v(17.98, -15.14) * mm});
            skLineSegment(sketch, "E145", {"start": v(17.98, -15.14) * mm, "end": v(18.93, -15.14) * mm});
            skLineSegment(sketch, "E146", {"start": v(18.93, -15.14) * mm, "end": v(19.74, -10.64) * mm});
            skLineSegment(sketch, "E147", {"start": v(19.74, -10.64) * mm, "end": v(18.4, -10.64) * mm});
            skLineSegment(sketch, "E148", {"start": v(18.4, -10.64) * mm, "end": v(16.9, -13.72) * mm});
            skLineSegment(sketch, "E149", {"start": v(16.9, -13.72) * mm, "end": v(16.7, -10.64) * mm});
            skLineSegment(sketch, "E150", {"start": v(16.7, -10.64) * mm, "end": v(15.4, -10.64) * mm});
            skLineSegment(sketch, "E151", {"start": v(-19.64, -11.98) * mm, "end": v(-18.64, -11.98) * mm});
            skLineSegment(sketch, "E152", {"start": v(-22.68, -13.7) * mm, "end": v(-21.68, -13.7) * mm});
            skFitSpline(sketch, "E153", {"points": [v(-18.64, -11.98) * mm, v(-18.73, -11.6) * mm, v(-19.2, -10.92) * mm, v(-19.9, -10.56) * mm, v(-20.84, -10.53) * mm, v(-21.52, -10.79) * mm, v(-22.01, -11.4) * mm, v(-22.08, -12.2) * mm, v(-21.66, -12.76) * mm, v(-21, -13.12) * mm, v(-20.18, -13.48) * mm, v(-19.96, -13.86) * mm, v(-20, -14.14) * mm, v(-20.21, -14.34) * mm, v(-20.6, -14.45) * mm, v(-21.06, -14.45) * mm, v(-21.42, -14.37) * mm, v(-21.63, -14.14) * mm, v(-21.68, -13.7) * mm], "startDerivative": vector(-0.37, 6.85) * mm, "endDerivative": vector(1.76, 9.54) * mm});
            skFitSpline(sketch, "E154", {"points": [v(-22.68, -13.7) * mm, v(-22.65, -14.08) * mm, v(-22.47, -14.56) * mm, v(-22.08, -14.92) * mm, v(-21.48, -15.16) * mm, v(-20.2, -15.19) * mm, v(-19.4, -14.7) * mm, v(-19.1, -14.23) * mm, v(-19.05, -13.6) * mm, v(-19.22, -13.14) * mm, v(-19.64, -12.76) * mm, v(-20.4, -12.42) * mm, v(-21, -12.09) * mm, v(-21.14, -11.88) * mm, v(-21.12, -11.58) * mm, v(-20.85, -11.34) * mm, v(-20.58, -11.29) * mm, v(-20.2, -11.34) * mm, v(-19.93, -11.45) * mm, v(-19.64, -11.98) * mm], "startDerivative": vector(0.18, -8.01) * mm, "endDerivative": vector(-2.84, -15.22) * mm});
            skSolve(sketch);
        }
        {
            var Q0;
            Q0=makeQuery(id+"F17.imprint","IMPRINT",FACE,{"disambiguationData":[TD([[makeQuery(id+"F17.imprint","IMPRINT",EDGE,{"derivedFrom":sQuery(id+"F17.wireOp",EDGE,"E62")}),-1.0]])]});
            cPlane(context, id + "F18", {"entities" : qUnion([Q0]), "cplaneType" : CPlaneType.OFFSET, "offset" : 0.5 * mm, "width" : 150 * mm, "height" : 150 * mm});
        }
        {
            var Q0;
            Q0=qCreatedBy(id+"F18.planeOp",FACE);
            var sketch = newSketch(context, id + "F19", { "sketchPlane" : qUnion([Q0])});
            skLineSegment(sketch, "E155.0", {"start": v(-13.82, 13.96) * mm, "end": v(-12.19, 20.46) * mm});
            skLineSegment(sketch, "E156.0", {"start": v(-12.19, 20.46) * mm, "end": v(-14.6, 23.76) * mm});
            skLineSegment(sketch, "E157.0", {"start": v(-14.6, 23.76) * mm, "end": v(-18.97, 23.76) * mm});
            skLineSegment(sketch, "E158.0", {"start": v(-18.97, 23.76) * mm, "end": v(-20.88, 17.84) * mm});
            skLineSegment(sketch, "E159.0", {"start": v(-20.88, 17.84) * mm, "end": v(-18.97, 13.96) * mm});
            skLineSegment(sketch, "E160.0", {"start": v(-18.97, 13.96) * mm, "end": v(-13.82, 13.96) * mm});
            skLineSegment(sketch, "E161.0", {"start": v(-12.5, 12.71) * mm, "end": v(-19.45, 12.71) * mm});
            skLineSegment(sketch, "E162.0", {"start": v(-19.45, 12.71) * mm, "end": v(-23.25, 7.69) * mm});
            skLineSegment(sketch, "E163.0", {"start": v(-23.25, 7.69) * mm, "end": v(-22.38, -8.4) * mm});
            skLineSegment(sketch, "E164.0", {"start": v(-22.38, -8.4) * mm, "end": v(-12.85, -8.4) * mm});
            skLineSegment(sketch, "E165.0", {"start": v(-12.85, -8.4) * mm, "end": v(-11.17, 4.8) * mm});
            skLineSegment(sketch, "E166.0", {"start": v(-11.17, 4.8) * mm, "end": v(-11.17, 10.03) * mm});
            skPoint(sketch, "E167.0", {"position": v(-11.83, 11.37) * mm});
            skLineSegment(sketch, "E168.0", {"start": v(-12.5, 12.71) * mm, "end": v(-11.17, 10.03) * mm});
            skSolve(sketch);
        }
        {
            var Q0;
            Q0 = qSketchRegion(id + "F19", true);
            var Q1;
            Q1=makeQuery(id+"F16.opExtrude","CAP_FACE",FACE,{"disambiguationData":[OSD([sQuery(id+"F15.wireOp",EDGE,"E48.0"),sQuery(id+"F15.wireOp",EDGE,"E49.0"),sQuery(id+"F15.wireOp",EDGE,"E50.0"),sQuery(id+"F15.wireOp",EDGE,"E51.0"),sQuery(id+"F15.wireOp",EDGE,"E52.0"),sQuery(id+"F15.wireOp",EDGE,"E53.0"),sQuery(id+"F15.wireOp",EDGE,"E54.0"),sQuery(id+"F15.wireOp",EDGE,"E55.0"),sQuery(id+"F15.wireOp",EDGE,"E56.0"),sQuery(id+"F15.wireOp",EDGE,"E58.0"),sQuery(id+"F15.wireOp",EDGE,"E59.0"),sQuery(id+"F15.wireOp",EDGE,"E60.0")])],"isStart":false});
            extrude(context, id + "F20", {"entities" : qUnion([Q0]), "operationType" : NewBodyOperationType.ADD, "endBound" : BoundingType.UP_TO_SURFACE, "oppositeDirection" : true, "endBoundEntityFace" : qUnion([Q1]), "depth" : 25 * mm});
        }
        {
            var Q0;
            Q0=qCreatedBy(id+"F18.planeOp",FACE);
            cPlane(context, id + "F21", {"entities" : qUnion([Q0]), "cplaneType" : CPlaneType.OFFSET, "offset" : 0.5 * mm, "width" : 150 * mm, "height" : 150 * mm});
        }
        {
            var Q0;
            Q0=qCreatedBy(id+"F21.planeOp",FACE);
            var sketch = newSketch(context, id + "F22", { "sketchPlane" : qUnion([Q0])});
            skLineSegment(sketch, "E169.0.0", {"start": v(4.16, 3.23) * mm, "end": v(5.19, 7.3) * mm});
            skLineSegment(sketch, "E169.0.1", {"start": v(5.19, 7.3) * mm, "end": v(-6.81, 7.3) * mm});
            skLineSegment(sketch, "E169.0.2", {"start": v(-6.81, 7.3) * mm, "end": v(-9.83, -7.39) * mm});
            skLineSegment(sketch, "E169.0.3", {"start": v(-9.83, -7.39) * mm, "end": v(2.03, -7.39) * mm});
            skLineSegment(sketch, "E169.0.4", {"start": v(2.03, -7.39) * mm, "end": v(2.86, -3.37) * mm});
            skLineSegment(sketch, "E169.0.5", {"start": v(2.86, -3.37) * mm, "end": v(-3.77, -3.37) * mm});
            skLineSegment(sketch, "E169.0.6", {"start": v(-3.77, -3.37) * mm, "end": v(-3.32, -1.85) * mm});
            skLineSegment(sketch, "E169.0.7", {"start": v(-3.32, -1.85) * mm, "end": v(3.16, -1.85) * mm});
            skLineSegment(sketch, "E169.0.8", {"start": v(3.16, -1.85) * mm, "end": v(4.1, 1.74) * mm});
            skLineSegment(sketch, "E169.0.9", {"start": v(4.1, 1.74) * mm, "end": v(-3, 1.74) * mm});
            skLineSegment(sketch, "E169.0.10", {"start": v(-3, 1.74) * mm, "end": v(-2.6, 3.23) * mm});
            skLineSegment(sketch, "E169.0.11", {"start": v(-2.6, 3.23) * mm, "end": v(4.16, 3.23) * mm});
            skLineSegment(sketch, "E170.0.0", {"start": v(31.95, 8.99) * mm, "end": v(-7.13, 8.99) * mm});
            skLineSegment(sketch, "E170.0.1", {"start": v(-7.13, 8.99) * mm, "end": v(-7.13, 7.99) * mm});
            skLineSegment(sketch, "E170.0.2", {"start": v(-7.13, 7.99) * mm, "end": v(31.95, 7.99) * mm});
            skLineSegment(sketch, "E170.0.3", {"start": v(31.95, 7.99) * mm, "end": v(31.95, 8.99) * mm});
            skLineSegment(sketch, "E171.0.0", {"start": v(11.74, 4.8) * mm, "end": v(11.1, 7.3) * mm});
            skLineSegment(sketch, "E171.0.1", {"start": v(11.1, 7.3) * mm, "end": v(6.97, 7.3) * mm});
            skLineSegment(sketch, "E171.0.2", {"start": v(6.97, 7.3) * mm, "end": v(8.31, 0.32) * mm});
            skLineSegment(sketch, "E171.0.3", {"start": v(8.31, 0.32) * mm, "end": v(2.35, -7.39) * mm});
            skLineSegment(sketch, "E171.0.4", {"start": v(2.35, -7.39) * mm, "end": v(7.16, -7.39) * mm});
            skLineSegment(sketch, "E171.0.5", {"start": v(7.16, -7.39) * mm, "end": v(9.14, -4.85) * mm});
            skLineSegment(sketch, "E171.0.6", {"start": v(9.14, -4.85) * mm, "end": v(9.52, -7.39) * mm});
            skLineSegment(sketch, "E171.0.7", {"start": v(9.52, -7.39) * mm, "end": v(14.1, -7.39) * mm});
            skLineSegment(sketch, "E171.0.8", {"start": v(14.1, -7.39) * mm, "end": v(12.74, -0.31) * mm});
            skLineSegment(sketch, "E171.0.9", {"start": v(12.74, -0.31) * mm, "end": v(18.8, 7.3) * mm});
            skLineSegment(sketch, "E171.0.10", {"start": v(18.8, 7.3) * mm, "end": v(13.63, 7.3) * mm});
            skLineSegment(sketch, "E171.0.11", {"start": v(13.63, 7.3) * mm, "end": v(11.74, 4.8) * mm});
            skLineSegment(sketch, "E172.0.0", {"start": v(26.97, -7.39) * mm, "end": v(31.46, 7.3) * mm});
            skLineSegment(sketch, "E172.0.1", {"start": v(31.46, 7.3) * mm, "end": v(19.77, 7.3) * mm});
            skLineSegment(sketch, "E172.0.2", {"start": v(19.77, 7.3) * mm, "end": v(15.14, -7.39) * mm});
            skLineSegment(sketch, "E172.0.3", {"start": v(15.14, -7.39) * mm, "end": v(26.97, -7.39) * mm});
            skLineSegment(sketch, "E173.0.0", {"start": v(-10.12, -7.88) * mm, "end": v(-10.12, -8.88) * mm});
            skLineSegment(sketch, "E173.0.1", {"start": v(-10.12, -8.88) * mm, "end": v(27.39, -8.88) * mm});
            skLineSegment(sketch, "E173.0.2", {"start": v(27.39, -8.88) * mm, "end": v(27.39, -7.88) * mm});
            skLineSegment(sketch, "E173.0.3", {"start": v(27.39, -7.88) * mm, "end": v(-10.12, -7.88) * mm});
            skLineSegment(sketch, "E174.0.0", {"start": v(-13.07, -12.6) * mm, "end": v(-13.89, -10.63) * mm});
            skLineSegment(sketch, "E174.0.1", {"start": v(-13.89, -10.63) * mm, "end": v(-14.91, -10.63) * mm});
            skLineSegment(sketch, "E174.0.2", {"start": v(-14.91, -10.63) * mm, "end": v(-13.57, -13.38) * mm});
            skLineSegment(sketch, "E174.0.3", {"start": v(-13.57, -13.38) * mm, "end": v(-14, -15.16) * mm});
            skLineSegment(sketch, "E174.0.4", {"start": v(-14, -15.16) * mm, "end": v(-13.01, -15.16) * mm});
            skLineSegment(sketch, "E174.0.5", {"start": v(-13.01, -15.16) * mm, "end": v(-12.7, -13.44) * mm});
            skLineSegment(sketch, "E174.0.6", {"start": v(-12.7, -13.44) * mm, "end": v(-10.61, -10.65) * mm});
            skLineSegment(sketch, "E174.0.7", {"start": v(-10.61, -10.65) * mm, "end": v(-11.7, -10.65) * mm});
            skLineSegment(sketch, "E174.0.8", {"start": v(-11.7, -10.65) * mm, "end": v(-13.07, -12.6) * mm});
            skLineSegment(sketch, "E175.0.0", {"start": v(-21.68, -13.7) * mm, "end": v(-22.68, -13.7) * mm});
            skFitSpline(sketch, "E175.0.1", {"points": [v(-22.68, -13.7) * mm, v(-22.68, -13.82) * mm, v(-22.67, -14.08) * mm, v(-22.52, -14.6) * mm, v(-22.07, -14.96) * mm, v(-21.48, -15.2) * mm, v(-20.18, -15.33) * mm, v(-19.36, -14.75) * mm, v(-19.07, -14.25) * mm, v(-19.01, -13.6) * mm, v(-19.18, -13.1) * mm, v(-19.64, -12.71) * mm, v(-20.38, -12.44) * mm, v(-21, -12.12) * mm, v(-21.15, -11.9) * mm, v(-21.18, -11.55) * mm, v(-20.85, -11.32) * mm, v(-20.58, -11.27) * mm, v(-20.18, -11.34) * mm, v(-19.93, -11.43) * mm, v(-19.6, -11.7) * mm, v(-19.64, -11.98) * mm]});
            skLineSegment(sketch, "E175.0.2", {"start": v(-19.64, -11.98) * mm, "end": v(-18.64, -11.98) * mm});
            skFitSpline(sketch, "E175.0.3", {"points": [v(-18.64, -11.98) * mm, v(-18.65, -11.87) * mm, v(-18.7, -11.56) * mm, v(-19.17, -10.85) * mm, v(-19.89, -10.5) * mm, v(-20.85, -10.49) * mm, v(-21.56, -10.72) * mm, v(-22.08, -11.37) * mm, v(-22.2, -12.24) * mm, v(-21.67, -12.8) * mm, v(-21.04, -13.15) * mm, v(-20.14, -13.4) * mm, v(-19.92, -13.84) * mm, v(-19.97, -14.16) * mm, v(-20.2, -14.36) * mm, v(-20.6, -14.47) * mm, v(-21.05, -14.45) * mm, v(-21.44, -14.41) * mm, v(-21.67, -14.15) * mm, v(-21.7, -13.86) * mm, v(-21.68, -13.7) * mm]});
            skLineSegment(sketch, "E176.0.0", {"start": v(3.7, -11.5) * mm, "end": v(3.92, -10.64) * mm});
            skLineSegment(sketch, "E176.0.1", {"start": v(3.92, -10.64) * mm, "end": v(0.36, -10.64) * mm});
            skLineSegment(sketch, "E176.0.2", {"start": v(0.36, -10.64) * mm, "end": v(0.24, -11.5) * mm});
            skLineSegment(sketch, "E176.0.3", {"start": v(0.24, -11.5) * mm, "end": v(1.53, -11.5) * mm});
            skLineSegment(sketch, "E176.0.4", {"start": v(1.53, -11.5) * mm, "end": v(0.72, -15.22) * mm});
            skLineSegment(sketch, "E176.0.5", {"start": v(0.72, -15.22) * mm, "end": v(1.7, -15.22) * mm});
            skLineSegment(sketch, "E176.0.6", {"start": v(1.7, -15.22) * mm, "end": v(2.52, -11.5) * mm});
            skLineSegment(sketch, "E176.0.7", {"start": v(2.52, -11.5) * mm, "end": v(3.7, -11.5) * mm});
            skLineSegment(sketch, "E177.0.0", {"start": v(11.01, -11.38) * mm, "end": v(11.15, -10.64) * mm});
            skLineSegment(sketch, "E177.0.1", {"start": v(11.15, -10.64) * mm, "end": v(7.75, -10.64) * mm});
            skLineSegment(sketch, "E177.0.2", {"start": v(7.75, -10.64) * mm, "end": v(6.93, -15.18) * mm});
            skLineSegment(sketch, "E177.0.3", {"start": v(6.93, -15.18) * mm, "end": v(10.49, -15.18) * mm});
            skLineSegment(sketch, "E177.0.4", {"start": v(10.49, -15.18) * mm, "end": v(10.65, -14.37) * mm});
            skLineSegment(sketch, "E177.0.5", {"start": v(10.65, -14.37) * mm, "end": v(8, -14.37) * mm});
            skLineSegment(sketch, "E177.0.6", {"start": v(8, -14.37) * mm, "end": v(8.29, -13.12) * mm});
            skLineSegment(sketch, "E177.0.7", {"start": v(8.29, -13.12) * mm, "end": v(10.67, -13.12) * mm});
            skLineSegment(sketch, "E177.0.8", {"start": v(10.67, -13.12) * mm, "end": v(10.8, -12.38) * mm});
            skLineSegment(sketch, "E177.0.9", {"start": v(10.8, -12.38) * mm, "end": v(8.64, -12.38) * mm});
            skLineSegment(sketch, "E177.0.10", {"start": v(8.64, -12.38) * mm, "end": v(8.85, -11.38) * mm});
            skLineSegment(sketch, "E177.0.11", {"start": v(8.85, -11.38) * mm, "end": v(11.01, -11.38) * mm});
            skLineSegment(sketch, "E178.0.0", {"start": v(16.9, -13.72) * mm, "end": v(16.7, -10.64) * mm});
            skLineSegment(sketch, "E178.0.1", {"start": v(16.7, -10.64) * mm, "end": v(15.4, -10.64) * mm});
            skLineSegment(sketch, "E178.0.2", {"start": v(15.4, -10.64) * mm, "end": v(14.51, -15.15) * mm});
            skLineSegment(sketch, "E178.0.3", {"start": v(14.51, -15.15) * mm, "end": v(15.37, -15.15) * mm});
            skLineSegment(sketch, "E178.0.4", {"start": v(15.37, -15.15) * mm, "end": v(16.08, -11.5) * mm});
            skLineSegment(sketch, "E178.0.5", {"start": v(16.08, -11.5) * mm, "end": v(16.2, -15.14) * mm});
            skLineSegment(sketch, "E178.0.6", {"start": v(16.2, -15.14) * mm, "end": v(17.18, -15.14) * mm});
            skLineSegment(sketch, "E178.0.7", {"start": v(17.18, -15.14) * mm, "end": v(18.87, -11.55) * mm});
            skLineSegment(sketch, "E178.0.8", {"start": v(18.87, -11.55) * mm, "end": v(17.98, -15.14) * mm});
            skLineSegment(sketch, "E178.0.9", {"start": v(17.98, -15.14) * mm, "end": v(18.93, -15.14) * mm});
            skLineSegment(sketch, "E178.0.10", {"start": v(18.93, -15.14) * mm, "end": v(19.74, -10.64) * mm});
            skLineSegment(sketch, "E178.0.11", {"start": v(19.74, -10.64) * mm, "end": v(18.4, -10.64) * mm});
            skLineSegment(sketch, "E178.0.12", {"start": v(18.4, -10.64) * mm, "end": v(16.9, -13.72) * mm});
            skLineSegment(sketch, "E179.0.0", {"start": v(-6.76, -13.72) * mm, "end": v(-7.76, -13.72) * mm});
            skFitSpline(sketch, "E179.0.1", {"points": [v(-7.76, -13.72) * mm, v(-7.75, -13.83) * mm, v(-7.75, -14.1) * mm, v(-7.6, -14.6) * mm, v(-7.15, -14.97) * mm, v(-6.56, -15.22) * mm, v(-5.26, -15.34) * mm, v(-4.44, -14.76) * mm, v(-4.15, -14.26) * mm, v(-4.09, -13.6) * mm, v(-4.26, -13.12) * mm, v(-4.72, -12.72) * mm, v(-5.46, -12.45) * mm, v(-6.09, -12.13) * mm, v(-6.23, -11.9) * mm, v(-6.26, -11.56) * mm, v(-5.93, -11.33) * mm, v(-5.66, -11.28) * mm, v(-5.26, -11.35) * mm, v(-5, -11.44) * mm, v(-4.67, -11.7) * mm, v(-4.72, -11.99) * mm]});
            skLineSegment(sketch, "E179.0.2", {"start": v(-4.72, -11.99) * mm, "end": v(-3.72, -11.99) * mm});
            skFitSpline(sketch, "E179.0.3", {"points": [v(-3.72, -11.99) * mm, v(-3.73, -11.88) * mm, v(-3.78, -11.57) * mm, v(-4.24, -10.86) * mm, v(-4.96, -10.51) * mm, v(-5.92, -10.5) * mm, v(-6.64, -10.73) * mm, v(-7.16, -11.38) * mm, v(-7.27, -12.25) * mm, v(-6.74, -12.82) * mm, v(-6.11, -13.16) * mm, v(-5.21, -13.4) * mm, v(-5, -13.85) * mm, v(-5.05, -14.17) * mm, v(-5.29, -14.37) * mm, v(-5.68, -14.48) * mm, v(-6.13, -14.46) * mm, v(-6.52, -14.42) * mm, v(-6.75, -14.16) * mm, v(-6.79, -13.87) * mm, v(-6.76, -13.72) * mm]});
            skLineSegment(sketch, "E180.0.0", {"start": v(24.16, -13.7) * mm, "end": v(23.16, -13.7) * mm});
            skFitSpline(sketch, "E180.0.1", {"points": [v(23.16, -13.7) * mm, v(23.17, -13.82) * mm, v(23.17, -14.08) * mm, v(23.33, -14.6) * mm, v(23.77, -14.96) * mm, v(24.36, -15.2) * mm, v(25.66, -15.33) * mm, v(26.48, -14.75) * mm, v(26.77, -14.25) * mm, v(26.83, -13.6) * mm, v(26.66, -13.1) * mm, v(26.2, -12.71) * mm, v(25.46, -12.44) * mm, v(24.83, -12.12) * mm, v(24.69, -11.9) * mm, v(24.66, -11.55) * mm, v(24.99, -11.32) * mm, v(25.26, -11.27) * mm, v(25.66, -11.34) * mm, v(25.91, -11.43) * mm, v(26.25, -11.7) * mm, v(26.2, -11.98) * mm]});
            skLineSegment(sketch, "E180.0.2", {"start": v(26.2, -11.98) * mm, "end": v(27.2, -11.98) * mm});
            skFitSpline(sketch, "E180.0.3", {"points": [v(27.2, -11.98) * mm, v(27.2, -11.87) * mm, v(27.14, -11.56) * mm, v(26.68, -10.85) * mm, v(25.96, -10.5) * mm, v(25, -10.49) * mm, v(24.28, -10.72) * mm, v(23.76, -11.37) * mm, v(23.65, -12.24) * mm, v(24.18, -12.8) * mm, v(24.8, -13.15) * mm, v(25.7, -13.4) * mm, v(25.92, -13.84) * mm, v(25.87, -14.16) * mm, v(25.63, -14.36) * mm, v(25.24, -14.47) * mm, v(24.79, -14.45) * mm, v(24.4, -14.41) * mm, v(24.17, -14.15) * mm, v(24.13, -13.86) * mm, v(24.16, -13.7) * mm]});
            skLineSegment(sketch, "E181", {"start": v(-34.2, 5.38) * mm, "end": v(-35.45, 3) * mm});
            skLineSegment(sketch, "E182", {"start": v(-35.45, 3) * mm, "end": v(-24.02, -3.05) * mm});
            skLineSegment(sketch, "E183", {"start": v(-34.2, 5.38) * mm, "end": v(-24.9, 1.67) * mm});
            skLineSegment(sketch, "E184", {"start": v(-24.9, 1.67) * mm, "end": v(-19.66, 9.15) * mm});
            skLineSegment(sketch, "E185", {"start": v(-13.73, 5.36) * mm, "end": v(-21.63, -2.6) * mm});
            skArc(sketch, "E186", {"start": v(-24.02, -3.05) * mm, "mid": v(-22.78, -3.04) * mm, "end": v(-21.63, -2.6) * mm});
            skArc(sketch, "E187", {"start": v(-13.73, 5.36) * mm, "mid": v(-14.88, 10.1) * mm, "end": v(-19.66, 9.15) * mm});
            skLineSegment(sketch, "E188.0", {"start": v(25.32, 1.8) * mm, "end": v(22.44, 1.8) * mm});
            skLineSegment(sketch, "E189.0", {"start": v(22.44, 1.8) * mm, "end": v(21.14, -1.91) * mm});
            skLineSegment(sketch, "E190.0", {"start": v(23.97, -1.91) * mm, "end": v(25.32, 1.8) * mm});
            skLineSegment(sketch, "E191.0", {"start": v(21.14, -1.91) * mm, "end": v(23.97, -1.91) * mm});
            skSolve(sketch);
        }
        {
            var Q0;
            Q0=qCreatedBy(id+"F21.planeOp",FACE);
            cPlane(context, id + "F23", {"entities" : qUnion([Q0]), "cplaneType" : CPlaneType.OFFSET, "offset" : 0.5 * mm, "width" : 150 * mm, "height" : 150 * mm});
        }
        {
            var Q0;
            Q0=qCreatedBy(id+"F23.planeOp",FACE);
            var sketch = newSketch(context, id + "F24", { "sketchPlane" : qUnion([Q0])});
            skLineSegment(sketch, "E192", {"start": v(-14.9, 11.56) * mm, "end": v(-14.9, 13.3) * mm});
            skLineSegment(sketch, "E193", {"start": v(-14.9, 13.3) * mm, "end": v(-11.8, 13.3) * mm});
            skLineSegment(sketch, "E194", {"start": v(-11.8, 13.3) * mm, "end": v(-10.89, 11.45) * mm});
            skLineSegment(sketch, "E195", {"start": v(-10.89, 11.45) * mm, "end": v(-9.88, 11.45) * mm});
            skLineSegment(sketch, "E196", {"start": v(-9.88, 11.45) * mm, "end": v(-8.98, 7.07) * mm});
            skLineSegment(sketch, "E197", {"start": v(-8.98, 7.07) * mm, "end": v(-10.58, 7.07) * mm});
            skLineSegment(sketch, "E198", {"start": v(-10.58, 7.07) * mm, "end": v(-10.58, 4.85) * mm});
            skLineSegment(sketch, "E199", {"start": v(-10.58, 4.85) * mm, "end": v(-9.41, 3.03) * mm});
            skLineSegment(sketch, "E200", {"start": v(-9.41, 3.03) * mm, "end": v(-10.33, 2.05) * mm});
            skLineSegment(sketch, "E201", {"start": v(-10.33, 2.05) * mm, "end": v(-11.2, 2.51) * mm});
            skLineSegment(sketch, "E202", {"start": v(-11.2, 2.51) * mm, "end": v(-21.8, -6.6) * mm});
            skLineSegment(sketch, "E203", {"start": v(-21.8, -6.6) * mm, "end": v(-22, -7.16) * mm});
            skLineSegment(sketch, "E204", {"start": v(-22, -7.16) * mm, "end": v(-23.8, -7.16) * mm});
            skLineSegment(sketch, "E205", {"start": v(-23.8, -7.16) * mm, "end": v(-24.08, -6.6) * mm});
            skLineSegment(sketch, "E206", {"start": v(-24.08, -6.6) * mm, "end": v(-34.74, -0.18) * mm});
            skLineSegment(sketch, "E207", {"start": v(-34.74, -0.18) * mm, "end": v(-32.1, 4.6) * mm});
            skLineSegment(sketch, "E208", {"start": v(-32.1, 4.6) * mm, "end": v(-28.13, 3.02) * mm});
            skLineSegment(sketch, "E209", {"start": v(-28.13, 3.02) * mm, "end": v(-30.32, -1.3) * mm});
            skLineSegment(sketch, "E210", {"start": v(-30.32, -1.3) * mm, "end": v(-24.6, -4.92) * mm});
            skLineSegment(sketch, "E211", {"start": v(-24.6, -4.92) * mm, "end": v(-21.08, -4.92) * mm});
            skLineSegment(sketch, "E212", {"start": v(-21.08, -4.92) * mm, "end": v(-12.43, 3.07) * mm});
            skLineSegment(sketch, "E213", {"start": v(-12.43, 3.07) * mm, "end": v(-12.25, 5.96) * mm});
            skArc(sketch, "E214", {"start": v(-12.25, 5.96) * mm, "mid": v(-12.63, 9.2) * mm, "end": v(-14.9, 11.56) * mm});
            skSolve(sketch);
        }
        {
            var Q0;
            Q0 = qSketchRegion(id + "F22", true);
            var Q1;
            Q1=makeQuery(id+"F16.opExtrude","CAP_FACE",FACE,{"disambiguationData":[OSD([sQuery(id+"F15.wireOp",EDGE,"E48.0"),sQuery(id+"F15.wireOp",EDGE,"E49.0"),sQuery(id+"F15.wireOp",EDGE,"E50.0"),sQuery(id+"F15.wireOp",EDGE,"E51.0"),sQuery(id+"F15.wireOp",EDGE,"E52.0"),sQuery(id+"F15.wireOp",EDGE,"E53.0"),sQuery(id+"F15.wireOp",EDGE,"E54.0"),sQuery(id+"F15.wireOp",EDGE,"E55.0"),sQuery(id+"F15.wireOp",EDGE,"E56.0"),sQuery(id+"F15.wireOp",EDGE,"E58.0"),sQuery(id+"F15.wireOp",EDGE,"E59.0"),sQuery(id+"F15.wireOp",EDGE,"E60.0")])],"isStart":false});
            extrude(context, id + "F25", {"entities" : qUnion([Q0]), "operationType" : NewBodyOperationType.ADD, "endBound" : BoundingType.UP_TO_SURFACE, "oppositeDirection" : true, "endBoundEntityFace" : qUnion([Q1]), "depth" : 2 * mm});
        }
        {
            var Q0;
            Q0 = qSketchRegion(id + "F24", true);
            var Q1;
            Q1=makeQuery(id+"F16.opExtrude","CAP_FACE",FACE,{"disambiguationData":[OSD([sQuery(id+"F15.wireOp",EDGE,"E48.0"),sQuery(id+"F15.wireOp",EDGE,"E49.0"),sQuery(id+"F15.wireOp",EDGE,"E50.0"),sQuery(id+"F15.wireOp",EDGE,"E51.0"),sQuery(id+"F15.wireOp",EDGE,"E52.0"),sQuery(id+"F15.wireOp",EDGE,"E53.0"),sQuery(id+"F15.wireOp",EDGE,"E54.0"),sQuery(id+"F15.wireOp",EDGE,"E55.0"),sQuery(id+"F15.wireOp",EDGE,"E56.0"),sQuery(id+"F15.wireOp",EDGE,"E58.0"),sQuery(id+"F15.wireOp",EDGE,"E59.0"),sQuery(id+"F15.wireOp",EDGE,"E60.0")])],"isStart":false});
            extrude(context, id + "F26", {"entities" : qUnion([Q0]), "operationType" : NewBodyOperationType.ADD, "endBound" : BoundingType.UP_TO_SURFACE, "oppositeDirection" : true, "endBoundEntityFace" : qUnion([Q1]), "depth" : 25 * mm});
        }
    });
